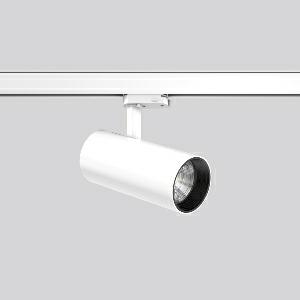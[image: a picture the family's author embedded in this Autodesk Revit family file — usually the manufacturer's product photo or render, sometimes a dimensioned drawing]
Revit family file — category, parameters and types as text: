
# Revit family: deecos_s_mini_742209_002_3_76_64c2
name_source: partatom
category: Lighting Fixtures
units: mm (PartAtom-declared; Revit-internal decimal feet)

## family parameters
Cut with Voids When Loaded = No
Host = Face
Light Source = No
Part Type = Normal
Room Calculation Point = No
Round Connector Dimension = Use Diameter
Shared = No

## types (1)
- DEECOS S mini (1 x LED Modul 935, 3300 lm, 3500)
    Apparent Load = 29 VA
    Approval mark = CE
    CIE Flux Codes = 80 99 100 100 100
    Color Rendering = 92
    Color Temperature = 3500
    Default Elevation = 1800 mm
    Description = Series: DEECOS S mini
LED surface-mounted projector in modern design with no visible cooling ribs. Housing: die-cast aluminium, powder-coated. Rotation range: 356°. Swivel range: 90°. Black plastic ring and recessed LED to prevent glare from the side. Optical assembly with lens made of plastic (polycarbonate) for the best homogeneous light distribution - can be changed without tools. Best colour rendering index Ra>90. With adapter for RZB 3-circuit DALI tracks. Suitable for Track on ceiling, Wall track. High quality converter without flickering and stroboscopic effect. The following accessories can be mounted without use of tools: interchangeable lenses, decorative glasses, honeycomb louvre, clear and frosted diffusers, white interchangeable plastic ring. 
Colour: traffic white, matt (RAL 9016)
Diameter: 87 mm
Height: 214 mm
Lamp: LED
Socket: without socket
Colour temperature: 3500K
Colour rendering index (CRI): 92
System power: 29 W
Rated luminous flux: 3300 lm
Luminous efficiency: 114 lm/W
Control gear: Converter, dimmable, DALI
Protection class: I
Type of protection: IP 20
    Height = 214 mm
    Lamp = 1 x LED Modul 935
    Lamp Light Flux = 3300 lm
    Lamp count = 1
    Length = 87 mm
    Lifetime = 50000 h
    Luminous efficacy = 114 lm/W
    Manufacturer = RZB
    ModVariant = No
    Model = 742209.002.3.76
    Mounting Place = Ceiling
    Mounting Type = Rail mounted
    Number of Poles = 1
    OnlyDefault = Yes
    Power Factor = 1
    Product Name = DEECOS S mini
    Product group = Track mounted projectors
    ProductGroupID = 301
    Protection Class = Protection class I
    Protection Degree = IP 20
    RLX_Detail_Level = 1
    RLX_Emergency_Light_Flux = 0 lm
    RLX_Emergency_Type = 0
    RLX_Emergency_Type_DB = No
    RlxData = <blob elided: 35593 chars, md5=b57e369a>
    Socket = socket
    Standby Power = 0 W
    System Light Flux = 3300 lm
    System Power = 29 W
    Type Comments = Product without accessories
    Type Image = 741930.002.jpg
    URL = http://relux.com
    VarID = ---
    Voltage = 230 V
    Voltage Range = 220-240 V
    Weight = 0.00 kg
    Width = 0 mm  [stored 0 ft]

note: [stored X ft] marks values corroborated as IEEE doubles in the binary element streams (Revit-internal decimal feet)

## geometry (parser evidence)
native form markers: Blend x4, Sweep x12
no freeform markers — native parametric forms only
